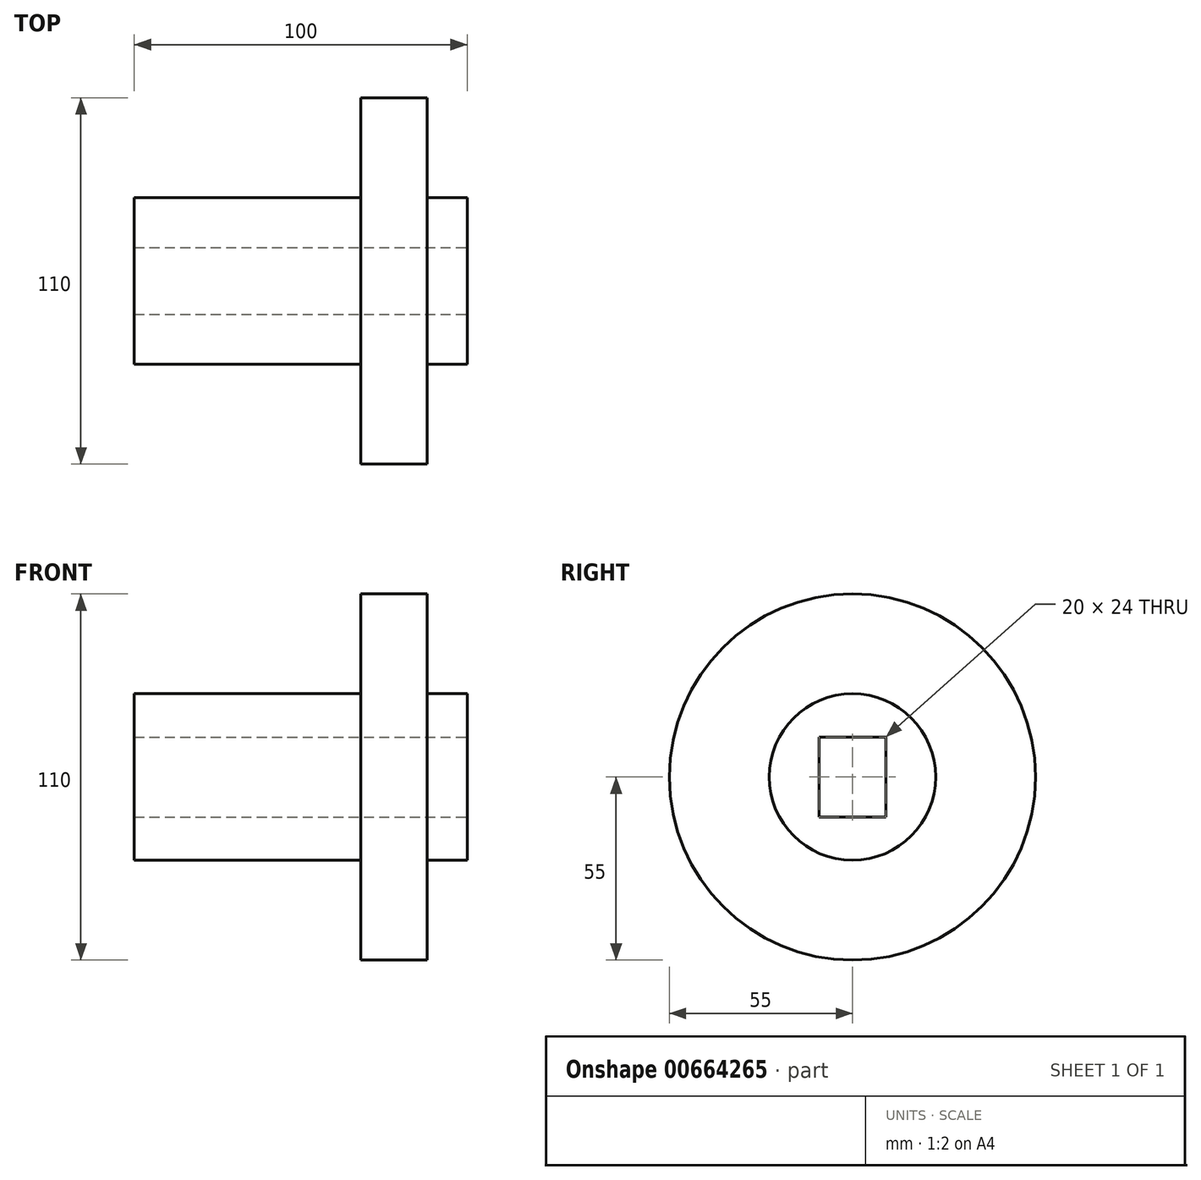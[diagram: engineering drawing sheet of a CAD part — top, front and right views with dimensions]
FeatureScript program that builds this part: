
annotation { "Feature Type Name" : "Feature", "Feature Type Description" : "" }
export const myFeature = defineFeature(function(context is Context, id is Id, definition is map)
    precondition{}
    {
        {
            var Q0;
            Q0=qCreatedBy(makeId("Front.planeOp"),FACE);
            var sketch = newSketch(context, id + "F0", { "sketchPlane" : qUnion([Q0])});
            skLineSegment(sketch, "E0", {"start": v(0, 0) * mm, "end": v(100, 0) * mm});
            skLineSegment(sketch, "E1", {"start": v(100, 0) * mm, "end": v(100, 25) * mm});
            skLineSegment(sketch, "E2", {"start": v(100, 25) * mm, "end": v(88, 25) * mm});
            skLineSegment(sketch, "E3", {"start": v(88, 25) * mm, "end": v(88, 55) * mm});
            skLineSegment(sketch, "E4", {"start": v(88, 55) * mm, "end": v(68, 55) * mm});
            skLineSegment(sketch, "E5", {"start": v(68, 55) * mm, "end": v(68, 25) * mm});
            skLineSegment(sketch, "E6", {"start": v(68, 25) * mm, "end": v(0, 25) * mm});
            skLineSegment(sketch, "E7", {"start": v(0, 25) * mm, "end": v(0, 0) * mm});
            skSolve(sketch);
        }
        {
            var Q0;
            Q0 = qSketchRegion(id + "F0", true);
            var Q1;
            Q1=sQuery(id+"F0.wireOp",EDGE,"E0");
            revolve(context, id + "F1", {"entities" : qUnion([Q0]), "axis" : qUnion([Q1]), "revolveType" : RevolveType.FULL});
        }
        {
            var Q0;
            Q0=makeQuery(id+"F1.opRevolve","SWEPT_FACE",FACE,{"disambiguationData":[OSD([sQuery(id+"F0.wireOp",EDGE,"E1")])]});
            var sketch = newSketch(context, id + "F2", { "sketchPlane" : qUnion([Q0])});
            skLineSegment(sketch, "E8", {"start": v(-10, -12) * mm, "end": v(-10, 12) * mm});
            skLineSegment(sketch, "E9", {"start": v(-10, 12) * mm, "end": v(10, 12) * mm});
            skLineSegment(sketch, "E10", {"start": v(10, 12) * mm, "end": v(10, -12) * mm});
            skLineSegment(sketch, "E11", {"start": v(10, -12) * mm, "end": v(-10, -12) * mm});
            skLineSegment(sketch, "E12", {"start": v(10, -12) * mm, "end": v(-10, 12) * mm, "construction": true});
            skLineSegment(sketch, "E13", {"start": v(10, 12) * mm, "end": v(-10, -12) * mm, "construction": true});
            skSolve(sketch);
        }
        {
            var Q0;
            Q0 = qSketchRegion(id + "F2", true);
            extrude(context, id + "F3", {"entities" : qUnion([Q0]), "operationType" : NewBodyOperationType.REMOVE, "endBound" : BoundingType.THROUGH_ALL, "oppositeDirection" : true, "depth" : 25 * mm, "offsetDistance" : 25 * mm});
        }
    });
